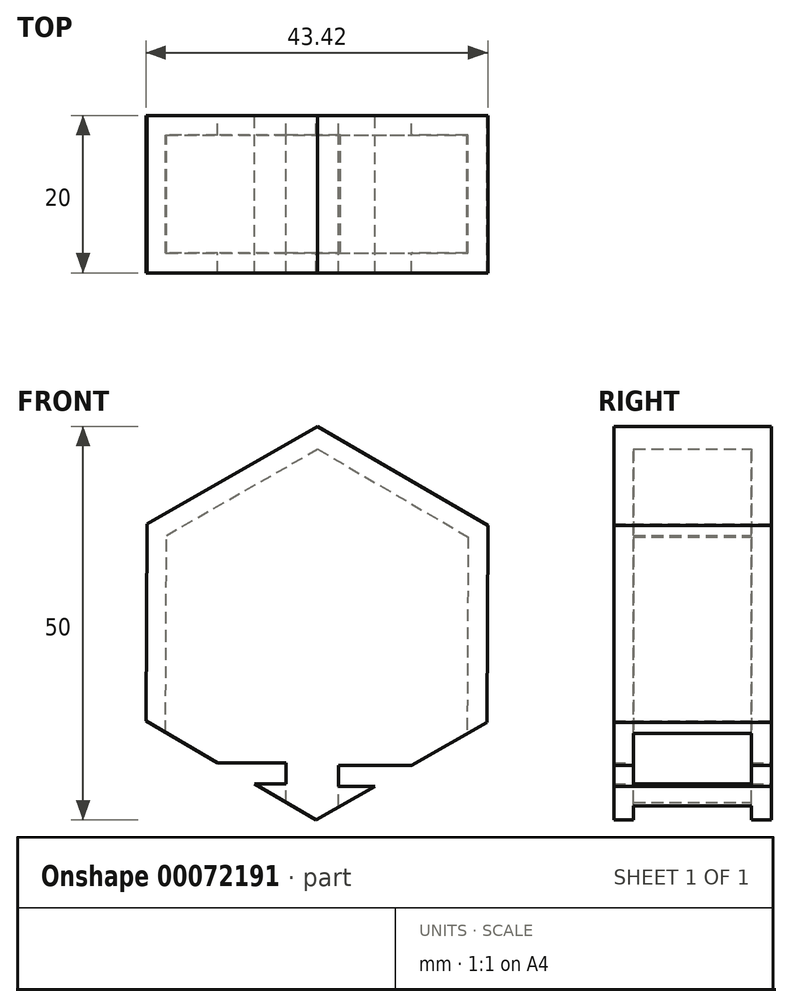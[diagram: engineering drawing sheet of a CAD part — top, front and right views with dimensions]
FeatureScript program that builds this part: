
annotation { "Feature Type Name" : "Feature", "Feature Type Description" : "" }
export const myFeature = defineFeature(function(context is Context, id is Id, definition is map)
    precondition{}
    {
        {
            var Q0;
            Q0=qCreatedBy(makeId("Front.planeOp"),FACE);
            var sketch = newSketch(context, id + "F0", { "sketchPlane" : qUnion([Q0])});
            skLineSegment(sketch, "E0.0", {"start": v(21.6, -12.6) * mm, "end": v(12, -18.08) * mm});
            skLineSegment(sketch, "E0.1", {"start": v(-0.11, -25) * mm, "end": v(-7.94, -20.43) * mm});
            skLineSegment(sketch, "E0.2", {"start": v(-21.7, -12.4) * mm, "end": v(-21.6, 12.6) * mm});
            skLineSegment(sketch, "E0.3", {"start": v(-21.6, 12.6) * mm, "end": v(0.11, 25) * mm});
            skLineSegment(sketch, "E0.4", {"start": v(0.11, 25) * mm, "end": v(21.7, 12.4) * mm});
            skLineSegment(sketch, "E0.5", {"start": v(21.7, 12.4) * mm, "end": v(21.6, -12.6) * mm});
            skLineSegment(sketch, "E1", {"start": v(-7.94, -20.43) * mm, "end": v(-3.94, -20.43) * mm});
            skLineSegment(sketch, "E2", {"start": v(-3.94, -20.43) * mm, "end": v(-3.94, -17.72) * mm});
            skLineSegment(sketch, "E3", {"start": v(-3.94, -17.72) * mm, "end": v(-12.6, -17.72) * mm});
            skLineSegment(sketch, "E4", {"start": v(7.38, -20.72) * mm, "end": v(2.73, -20.72) * mm});
            skLineSegment(sketch, "E5", {"start": v(2.73, -20.72) * mm, "end": v(2.73, -18.08) * mm});
            skLineSegment(sketch, "E6", {"start": v(2.73, -18.08) * mm, "end": v(12, -18.08) * mm});
            skLineSegment(sketch, "E7.trimOffspring", {"start": v(-12.6, -17.72) * mm, "end": v(-21.7, -12.4) * mm});
            skLineSegment(sketch, "E8.trimOffspring", {"start": v(7.38, -20.72) * mm, "end": v(-0.11, -25) * mm});
            skSolve(sketch);
        }
        {
            var Q0;
            Q0=makeQuery(id+"F0.imprint","IMPRINT",FACE,{"disambiguationData":[TD([[makeQuery(id+"F0.imprint","IMPRINT",EDGE,{"derivedFrom":sQuery(id+"F0.wireOp",EDGE,"E0.0")}),-1.0]])]});
            extrude(context, id + "F1", {"entities" : qUnion([Q0]), "depth" : 20 * mm});
        }
        {
            var Q0;
            Q0=makeQuery(id+"F1.opExtrude","SWEPT_FACE",FACE,{"disambiguationData":[OSD([sQuery(id+"F0.wireOp",EDGE,"E0.0")])]});
            var Q1;
            Q1=makeQuery(id+"F1.opExtrude","SWEPT_FACE",FACE,{"disambiguationData":[OSD([sQuery(id+"F0.wireOp",EDGE,"E6")])]});
            var Q2;
            Q2=makeQuery(id+"F1.opExtrude","SWEPT_FACE",FACE,{"disambiguationData":[OSD([sQuery(id+"F0.wireOp",EDGE,"E3")])]});
            var Q3;
            Q3=makeQuery(id+"F1.opExtrude","SWEPT_FACE",FACE,{"disambiguationData":[OSD([sQuery(id+"F0.wireOp",EDGE,"E7.trimOffspring")])]});
            var Q4;
            Q4=makeQuery(id+"F1.opExtrude","SWEPT_FACE",FACE,{"disambiguationData":[OSD([sQuery(id+"F0.wireOp",EDGE,"E2")])]});
            var Q5;
            Q5=makeQuery(id+"F1.opExtrude","SWEPT_FACE",FACE,{"disambiguationData":[OSD([sQuery(id+"F0.wireOp",EDGE,"E0.1")])]});
            var Q6;
            Q6=makeQuery(id+"F1.opExtrude","SWEPT_FACE",FACE,{"disambiguationData":[OSD([sQuery(id+"F0.wireOp",EDGE,"E8.trimOffspring")])]});
            var Q7;
            Q7=makeQuery(id+"F1.opExtrude","SWEPT_FACE",FACE,{"disambiguationData":[OSD([sQuery(id+"F0.wireOp",EDGE,"E5")])]});
            shell(context, id + "F2", {"entities" : qUnion([Q0, Q1, Q2, Q3, Q4, Q5, Q6, Q7]), "thickness" : 2.5 * mm});
        }
    });
